# Revit family: 1602-Swing-Up-Arm-Wood_DoorKing
name_source: partatom
category: Parking
units: mm (PartAtom-declared; Revit-internal decimal feet)

## family parameters
Always vertical = No
Classification Number = 23.15.10.14.24.24
Cut with Voids When Loaded = No
Shared = No
Work Plane-Based = No

## types (1)
- ByType
    Arm Length = 20' - 0"
    Arm Material = Metal - Aluminum - Anodized - White
    Assembly Code = E1030200
    Battery Backup = No
    Building Codes = http://www.doorking.com
    Description = Parking Gate Operator as Specified in 11 12 33
    Expected Lifespan (Years) = 0
    Fan Kit = No
    Foam Padding Kit = No
    Heater Kit = No
    Keynote = 11 12 33
    Maintenance Schedule (Months) = 0
    Manufacturer = DoorKing
    Manufacturer Fax = 310-641-1586
    Manufacturer Website = http://www.doorking.com
    Model = As Specified in 11 12 33
    Motor Amperage = 4.6
    Motor HP = 0.5
    Motor Phases = 1
    Motor Voltage = 230
    Operator Material = Metal - Steel - Galvanized - Painted White
    Product Data = http://www.arcat.com
    Product Properties = http://www.arcat.com
    Sales Information = http://dkslocator.com
    Send Message = http://www.arcat.com
    Specification = http://www.arcat.com
    Test Data = http://www.doorking.com
    Traffic Light = No
    URL = http://www.doorking.com
    Warranty Duration (Years) = 0

## geometry (parser evidence)
native form markers: Blend x28, Sweep x18
no freeform markers — native parametric forms only
